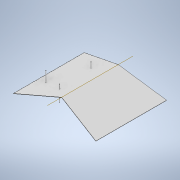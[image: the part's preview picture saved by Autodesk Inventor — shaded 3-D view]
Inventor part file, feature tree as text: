
AUTODESK INVENTOR PART (.ipt)
format: ipt  version: 2022.1 (Build 261234000, 234)  size: 119,808 bytes
history: native  units: in
note: dims shown in document units (in); Inventor stores cm internally (conversion verified against a paired STEP export)
features: sketch x3, extrude x3, plane x2
ambient origin geometry x8: Origin, YZ Plane, XZ Plane, XY Plane, X Axis, Y Axis, Z Axis, Center Point
bodies: Body1 (feature_tree)
feature tree (8):
  plane  "Work Plane3"
  sketch  "Sketch5"  dims[d11=0.1267in d14=216.0in]
  plane  "Work Plane4"
  sketch  "Sketch6"  dims[d15=166.0in d18=270.0in]
  extrude  "Extrusion3"  Depth=216.0in
  extrude  "Extrusion4"  Depth=270.0in
  extrude  "Extrusion5"  Depth=216.0in
  sketch  "Sketch7"  dims[d19=-0.1267in d20=216.0in d21=270.0in d22=166.0in d23=1.0in d24=0.0in d25=1.0in d26=0.0in d27=2.0in d28=60.0in d29=0.0in]
